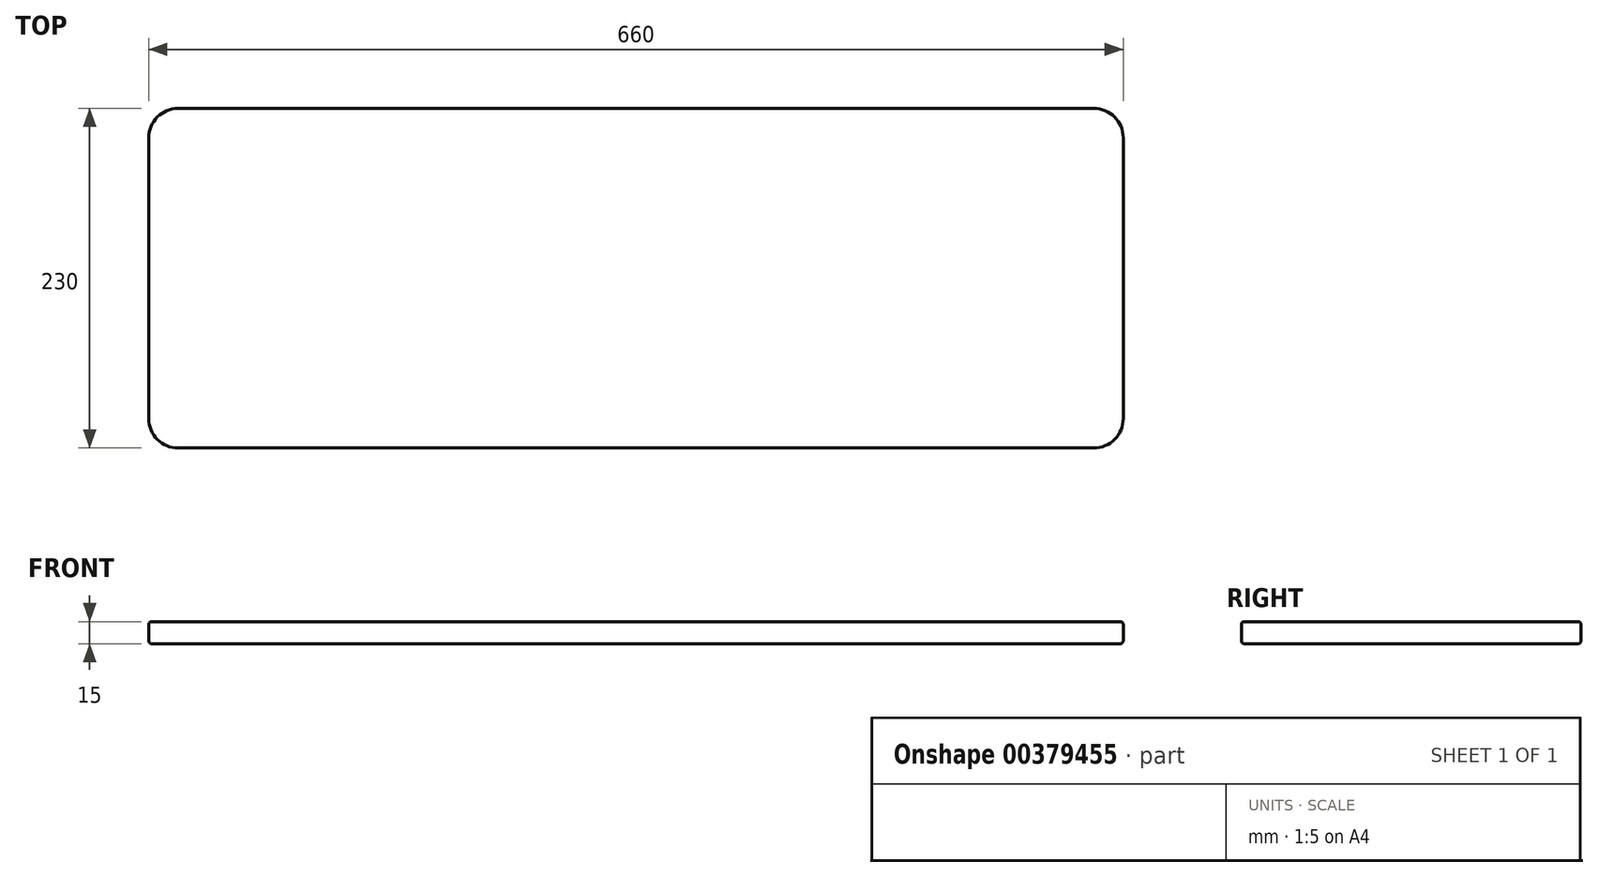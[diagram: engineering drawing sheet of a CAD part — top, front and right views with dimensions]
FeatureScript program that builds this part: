
annotation { "Feature Type Name" : "Feature", "Feature Type Description" : "" }
export const myFeature = defineFeature(function(context is Context, id is Id, definition is map)
    precondition{}
    {
        {
            var Q0;
            Q0=qCreatedBy(makeId("Top.planeOp"),FACE);
            var sketch = newSketch(context, id + "F0", { "sketchPlane" : qUnion([Q0])});
            skLineSegment(sketch, "E0.bottom", {"start": v(-330, 115) * mm, "end": v(330, 115) * mm});
            skLineSegment(sketch, "E0.top", {"start": v(-330, -115) * mm, "end": v(330, -115) * mm});
            skLineSegment(sketch, "E0.left", {"start": v(-330, 115) * mm, "end": v(-330, -115) * mm});
            skLineSegment(sketch, "E0.right", {"start": v(330, 115) * mm, "end": v(330, -115) * mm});
            skPoint(sketch, "E0.middle", {"position": v(0, 0) * mm});
            skSolve(sketch);
        }
        {
            var Q0;
            Q0=makeQuery(id+"F0.imprint","IMPRINT",FACE,{"disambiguationData":[TD([[makeQuery(id+"F0.imprint","IMPRINT",EDGE,{"derivedFrom":sQuery(id+"F0.wireOp",EDGE,"E0.bottom")}),-1.0]])]});
            extrude(context, id + "F1", {"entities" : qUnion([Q0]), "depth" : 15 * mm});
        }
        {
            var Q0;
            Q0=makeQuery(id+"F1.opExtrude","SWEPT_EDGE",EDGE,{"disambiguationData":[OSD([sQuery(id+"F0.wireOp",EDGE,"E0.top"),sQuery(id+"F0.wireOp",EDGE,"E0.right")])]});
            var Q1;
            Q1=makeQuery(id+"F1.opExtrude","SWEPT_EDGE",EDGE,{"disambiguationData":[OSD([sQuery(id+"F0.wireOp",EDGE,"E0.bottom"),sQuery(id+"F0.wireOp",EDGE,"E0.right")])]});
            var Q2;
            Q2=makeQuery(id+"F1.opExtrude","SWEPT_EDGE",EDGE,{"disambiguationData":[OSD([sQuery(id+"F0.wireOp",EDGE,"E0.top"),sQuery(id+"F0.wireOp",EDGE,"E0.left")])]});
            var Q3;
            Q3=makeQuery(id+"F1.opExtrude","SWEPT_EDGE",EDGE,{"disambiguationData":[OSD([sQuery(id+"F0.wireOp",EDGE,"E0.bottom"),sQuery(id+"F0.wireOp",EDGE,"E0.left")])]});
            fillet(context, id + "F2", {"entities" : qUnion([Q0, Q1, Q2, Q3]), "radius" : 20 * mm, "tangentPropagation" : true, "allowEdgeOverflow" : false});
        }
        {
            var Q0;
            Q0=makeQuery(id+"F1.opExtrude","CAP_FACE",FACE,{"disambiguationData":[OSD([sQuery(id+"F0.wireOp",EDGE,"E0.bottom"),sQuery(id+"F0.wireOp",EDGE,"E0.top"),sQuery(id+"F0.wireOp",EDGE,"E0.left"),sQuery(id+"F0.wireOp",EDGE,"E0.right")])],"isStart":false});
            var Q1;
            Q1=makeQuery(id+"F1.opExtrude","CAP_FACE",FACE,{"disambiguationData":[OSD([sQuery(id+"F0.wireOp",EDGE,"E0.bottom"),sQuery(id+"F0.wireOp",EDGE,"E0.top"),sQuery(id+"F0.wireOp",EDGE,"E0.left"),sQuery(id+"F0.wireOp",EDGE,"E0.right")])],"isStart":true});
            fillet(context, id + "F3", {"entities" : qUnion([Q0, Q1]), "radius" : 2 * mm, "tangentPropagation" : true, "allowEdgeOverflow" : false});
        }
    });
